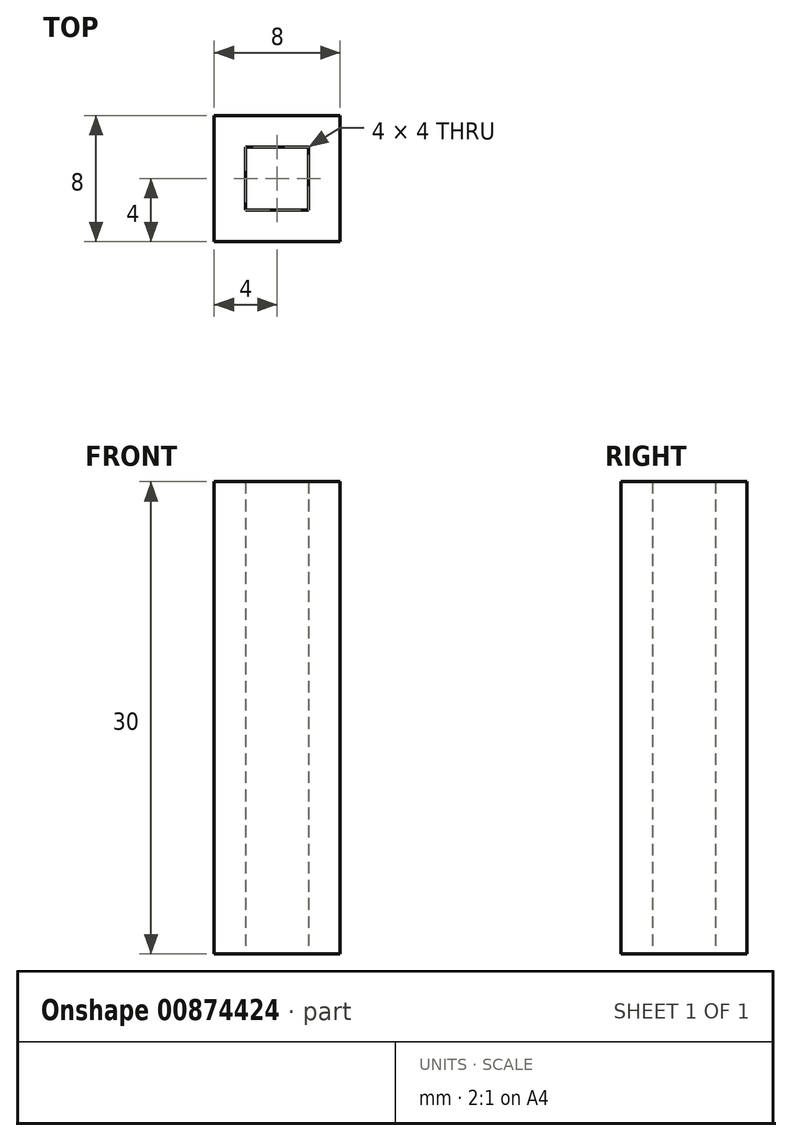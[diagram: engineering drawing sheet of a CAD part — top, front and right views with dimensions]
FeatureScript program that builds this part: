
annotation { "Feature Type Name" : "Feature", "Feature Type Description" : "" }
export const myFeature = defineFeature(function(context is Context, id is Id, definition is map)
    precondition{}
    {
        {
            var Q0;
            Q0=qCreatedBy(makeId("Top.planeOp"),FACE);
            var sketch = newSketch(context, id + "F0", { "sketchPlane" : qUnion([Q0])});
            skLineSegment(sketch, "E0.bottom", {"start": v(-4, 4) * mm, "end": v(4, 4) * mm});
            skLineSegment(sketch, "E0.top", {"start": v(-4, -4) * mm, "end": v(4, -4) * mm});
            skLineSegment(sketch, "E0.left", {"start": v(-4, 4) * mm, "end": v(-4, -4) * mm});
            skLineSegment(sketch, "E0.right", {"start": v(4, 4) * mm, "end": v(4, -4) * mm});
            skLineSegment(sketch, "E1.bottom", {"start": v(-2, 2) * mm, "end": v(2, 2) * mm});
            skLineSegment(sketch, "E1.top", {"start": v(-2, -2) * mm, "end": v(2, -2) * mm});
            skLineSegment(sketch, "E1.left", {"start": v(-2, 2) * mm, "end": v(-2, -2) * mm});
            skLineSegment(sketch, "E1.right", {"start": v(2, 2) * mm, "end": v(2, -2) * mm});
            skSolve(sketch);
        }
        {
            var Q0;
            Q0=makeQuery(id+"F0.imprint","IMPRINT",FACE,{"disambiguationData":[TD([[makeQuery(id+"F0.imprint","IMPRINT",EDGE,{"derivedFrom":sQuery(id+"F0.wireOp",EDGE,"E0.bottom")}),-1.0]])]});
            extrude(context, id + "F1", {"entities" : qUnion([Q0]), "depth" : 30 * mm, "offsetDistance" : 25 * mm});
        }
    });
